# Revit family: ASSA_ABLOY_DockLeveler_DL6120STA
name_source: partatom
category: Mechanical Equipment
units: mm (PartAtom-declared; Revit-internal decimal feet)

## family parameters
Always vertical = Yes
Classification = None
Cut with Voids When Loaded = No
Part Type = Normal
Room Calculation Point = No
Round Connector Dimension = Use Diameter
Shared = No
Work Plane-Based = No

## types (3) — shared parameters
DL6120STA_LipErgoSteel345 = DL6120STA_LevelerTop : DL6120STA_LipErgoSteelLL345
DL6120STA_LipSteel1000 = DL6120STA_LevelerTop : DL6120STA_LipSteelLL1000
DL6120STA_LipSteel500 = DL6120STA_LevelerTop : DL6120STA_LipSteelLL500

## per-type parameters (varying)
| type | LipType |
| DL6120STA_LipSteelLL500 | DL6120STA_LevelerTop : DL6120STA_LipSteelLL500 |
| DL6120STA_LipErgoSteelLL345 | DL6120STA_LevelerTop : DL6120STA_LipErgoSteelLL345 |
| DL6120STA_LipSteelLL1000 | DL6120STA_LevelerTop : DL6120STA_LipSteelLL1000 |

## geometry (parser evidence)
native form markers: Sweep x5
no freeform markers — native parametric forms only
